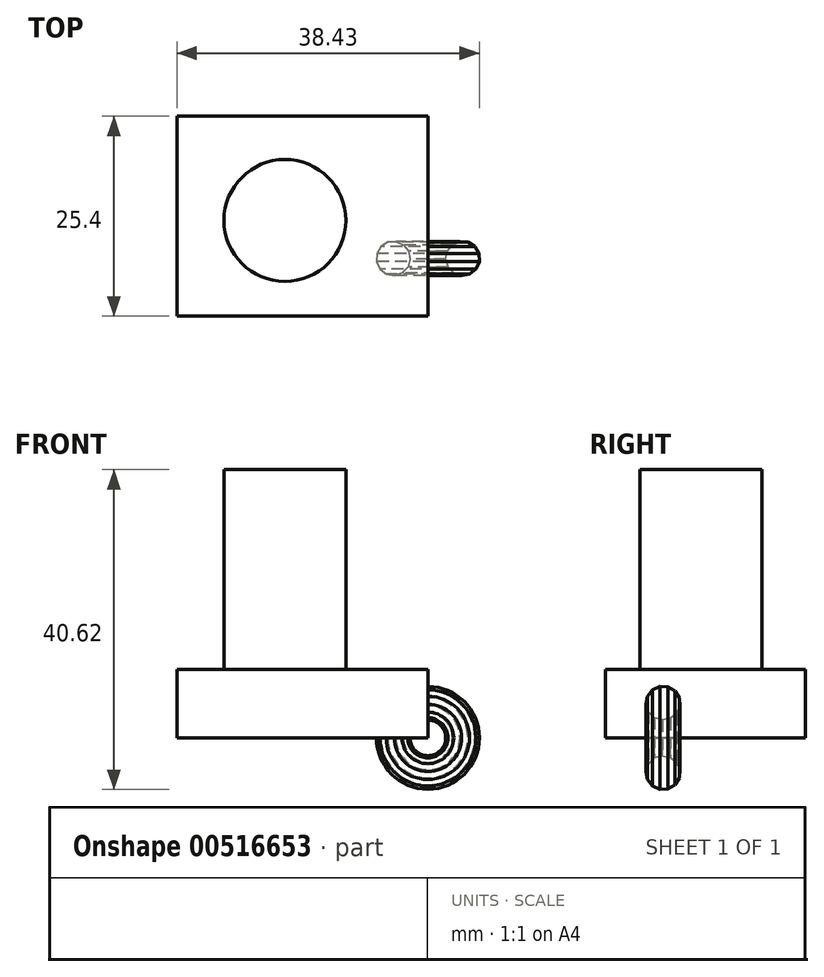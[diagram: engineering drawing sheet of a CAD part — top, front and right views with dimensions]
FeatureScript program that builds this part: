
annotation { "Feature Type Name" : "Feature", "Feature Type Description" : "" }
export const myFeature = defineFeature(function(context is Context, id is Id, definition is map)
    precondition{}
    {
        {
            var Q0;
            Q0=qCreatedBy(makeId("Front.planeOp"),FACE);
            var sketch = newSketch(context, id + "F0", { "sketchPlane" : qUnion([Q0])});
            skLineSegment(sketch, "E0", {"start": v(-19.5, 44.74) * mm, "end": v(12.4, 44.74) * mm});
            skLineSegment(sketch, "E1", {"start": v(12.4, 44.74) * mm, "end": v(12.4, 36.06) * mm});
            skLineSegment(sketch, "E2", {"start": v(-19.5, 44.74) * mm, "end": v(-19.5, 36.06) * mm});
            skLineSegment(sketch, "E3", {"start": v(-19.5, 36.06) * mm, "end": v(12.4, 36.06) * mm});
            skSolve(sketch);
        }
        {
            var Q0;
            Q0=makeQuery(id+"F0.imprint","IMPRINT",FACE,{"disambiguationData":[TD([[makeQuery(id+"F0.imprint","IMPRINT",EDGE,{"derivedFrom":sQuery(id+"F0.wireOp",EDGE,"E0")}),-1.0]])]});
            extrude(context, id + "F1", {"entities" : qUnion([Q0]), "depth" : 25.4 * mm, "offsetDistance" : 25.4 * mm});
        }
        {
            var Q0;
            Q0=makeQuery(id+"F1.opExtrude","SWEPT_FACE",FACE,{"disambiguationData":[OSD([sQuery(id+"F0.wireOp",EDGE,"E0")])]});
            var sketch = newSketch(context, id + "F2", { "sketchPlane" : qUnion([Q0])});
            skCircle(sketch, "E4", {"center": v(-5.76, -13.25) * mm, "radius": 7.75 * mm});
            skSolve(sketch);
        }
        {
            var Q0;
            Q0=makeQuery(id+"F2.imprint","IMPRINT",FACE,{"disambiguationData":[TD([[makeQuery(id+"F2.imprint","IMPRINT",EDGE,{"derivedFrom":sQuery(id+"F2.wireOp",EDGE,"E4")}),1.0]])]});
            extrude(context, id + "F3", {"entities" : qUnion([Q0]), "depth" : 25.4 * mm, "offsetDistance" : 25.4 * mm});
        }
        {
            var Q0;
            Q0=makeQuery(id+"F1.opExtrude","SWEPT_FACE",FACE,{"disambiguationData":[OSD([sQuery(id+"F0.wireOp",EDGE,"E1")])]});
            var sketch = newSketch(context, id + "F4", { "sketchPlane" : qUnion([Q0])});
            skCircle(sketch, "E5.cCircle", {"center": v(-18.07, 40.47) * mm, "radius": 2.1 * mm, "construction": true});
            skLineSegment(sketch, "E5.0", {"start": v(-15.94, 40.1) * mm, "end": v(-16.36, 39.16) * mm});
            skLineSegment(sketch, "E5.1", {"start": v(-16.36, 39.16) * mm, "end": v(-17.17, 38.51) * mm});
            skLineSegment(sketch, "E5.2", {"start": v(-17.17, 38.51) * mm, "end": v(-18.18, 38.32) * mm});
            skLineSegment(sketch, "E5.3", {"start": v(-18.18, 38.32) * mm, "end": v(-19.17, 38.61) * mm});
            skLineSegment(sketch, "E5.4", {"start": v(-19.17, 38.61) * mm, "end": v(-19.9, 39.34) * mm});
            skLineSegment(sketch, "E5.5", {"start": v(-19.9, 39.34) * mm, "end": v(-20.23, 40.32) * mm});
            skLineSegment(sketch, "E5.6", {"start": v(-20.23, 40.32) * mm, "end": v(-20.05, 41.34) * mm});
            skLineSegment(sketch, "E5.7", {"start": v(-20.05, 41.34) * mm, "end": v(-19.42, 42.16) * mm});
            skLineSegment(sketch, "E5.8", {"start": v(-19.42, 42.16) * mm, "end": v(-18.48, 42.6) * mm});
            skLineSegment(sketch, "E5.9", {"start": v(-18.48, 42.6) * mm, "end": v(-17.45, 42.54) * mm});
            skLineSegment(sketch, "E5.10", {"start": v(-17.45, 42.54) * mm, "end": v(-16.56, 42.02) * mm});
            skLineSegment(sketch, "E5.11", {"start": v(-16.56, 42.02) * mm, "end": v(-16.02, 41.14) * mm});
            skLineSegment(sketch, "E5.12", {"start": v(-16.02, 41.14) * mm, "end": v(-15.94, 40.1) * mm});
            skPoint(sketch, "E5.0.midPoint", {"position": v(-16.15, 39.63) * mm});
            skSolve(sketch);
        }
        {
            var Q0;
            Q0=makeQuery(id+"F4.imprint","IMPRINT",FACE,{"disambiguationData":[TD([[makeQuery(id+"F4.imprint","IMPRINT",EDGE,{"derivedFrom":sQuery(id+"F4.wireOp",EDGE,"E5.0")}),-1.0]])]});
            var Q1;
            Q1=makeQuery(id+"F1.opExtrude","SWEPT_EDGE",EDGE,{"disambiguationData":[OSD([sQuery(id+"F0.wireOp",EDGE,"E1"),sQuery(id+"F0.wireOp",EDGE,"E3")])]});
            revolve(context, id + "F5", {"operationType" : NewBodyOperationType.ADD, "entities" : qUnion([Q0]), "axis" : qUnion([Q1]), "revolveType" : RevolveType.FULL, "oppositeDirection" : true});
        }
    });
